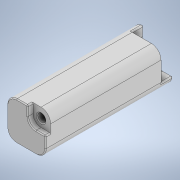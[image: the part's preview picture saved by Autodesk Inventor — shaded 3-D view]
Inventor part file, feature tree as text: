
AUTODESK INVENTOR PART (.ipt)
format: ipt  version: 2022 (Build 260153000, 153)  size: 181,760 bytes
history: native  units: mm
features: fillet x4, sketch x4, extrude x3, hole x1, chamfer x1
ambient origin geometry x8: Origin, YZ Plane, XZ Plane, XY Plane, X Axis, Y Axis, Z Axis, Center Point
bodies: Solid1 (feature_tree)
feature tree (13):
  extrude  "Extrusion1"  Depth=25.4mm
  extrude  "Extrusion2"  Depth=11.621mm
  extrude  "Extrusion3"  Depth=3.429mm TaperAngle=0.0deg
  hole  "Hole1"  [1 undecoded]
  fillet  "Fillet1"  Radius=7.938mm
  fillet  "Fillet2"  Radius=6.35mm
  fillet  "Fillet3"  Radius=6.35mm
  fillet  "Fillet4"  Radius=6.35mm
  chamfer  "Chamfer1"  Distance=0.794mm
  sketch  "Sketch1"  dims[d0=25.4mm d1=25.4mm]
  sketch  "Sketch2"  dims[d2=84.138mm d3=0.0mm d4=11.621mm]
  sketch  "Sketch3"  dims[d5=11.621mm d6=3.429mm d7=0.0mm]
  sketch  "Sketch4"  dims[d8=19.558mm d9=19.558mm d10=7.938mm d11=0.0mm d12=6.35mm d13=6.35mm d14=5.334mm d15=6.0mm d16=9.779mm d17=2.0mm d18=14.3117mm d19=8.0mm d20=20.594885mm d21=6.35mm d22=0.794mm d23=5.271mm d24=13.208mm d25=0.6mm d26=2.0mm d27=45.0deg]
note: 1 required parameter value undecoded (feature->parameter linkage not recoverable at this tier; creation-order binding heuristic only, values carry confidence <= 0.55)
